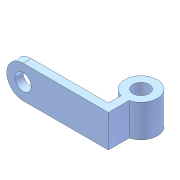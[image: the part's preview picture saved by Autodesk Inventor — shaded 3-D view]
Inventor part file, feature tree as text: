
AUTODESK INVENTOR PART (.ipt)
format: ipt  version: unknown  size: 184,832 bytes
history: native  units: mm
features: extrude x2, sketch x2, fillet x1
ambient origin geometry x8: Origin, YZ Plane, XZ Plane, XY Plane, X Axis, Y Axis, Z Axis, Center Point
feature tree (5):
  extrude  "Extrusion1"  Depth=4.0mm
  fillet  "Fillet1"  Radius=4.0mm
  extrude  "Extrusion2"  Depth=0.5mm
  sketch  "Sketch1"  dims[d0=2.0mm d1=4.0mm d2=4.0mm]
  sketch  "Sketch2"  dims[d3=10.0mm d4=0.5mm d5=1.0mm d6=2.0mm d7=4.0mm d8=0.0mm d9=2.0mm d10=2.0mm d11=4.0mm d12=0.0mm]
